# Revit family: QF_ELECTROLUXPROFESSIONAL_1LSNTG_WS6-28_E
name_source: partatom
category: Attrezzature speciali
units: mm (PartAtom-declared; Revit-internal decimal feet)

## family parameters
Basato su piano di lavoro = No
Condiviso = No
Punto di calcolo locali = No
Quota connettore circolare = Usa diametro
Sempre verticale = Sì
Taglio con vuoti quando caricato = No
Tipo di parte = Normale

## types (36) — shared parameters
Depth = 1030 mm  [stored 3.37927 ft]
Depth Actual = 1030 mm  [stored 3.37927 ft]
Height = 1430.8 mm  [stored 4.69423 ft]
Height Actual = 1430 mm  [stored 4.6916 ft]
Latent Heat Output = 0.0
Length Actual = 830 mm  [stored 2.7231 ft]
Modello = WS6-28
Produttore = Electrolux Professional
Sensible Heat Output = 0.0
URL = www.electroluxprofessional.com
Weight = 262
Width = 830 mm  [stored 2.7231 ft]
zero-valued in all types: Gas KW, Prospetto di default, Steam Pounds per Hour

## per-type parameters (varying)
| type | Cycle | Descrizione | Item Number | Phase | Volts | Watts |
| 9867930109 | 50 Hz | WASHER WS6-28 28KG EL 18KW 380-415/50/3N COMPASS PRO 6H01 ML 2xWATER POWDER+5xLIQ. VALV.OPEN SILVER 2.I/O DISCON. STOP | 1LSP3U | 3 | 415 V | 18800 W |
| 9867930201 | 50 Hz | WASHER WS6-28 28KG EL 18KW 380-415/50/3N COMPASS PRO 6G01 CH-EN 2xWATER POWDER EL.VALV.OPEN SILVER DISCON. STOP | 1LA23U | 3 | 415 V | 18800 W |
| 9867930106 | 50 Hz | WASHER WS6-28 28KG EL 18KW 380-415/50/3N COMPASS PRO 6H12 ML 2xWATER POWDER+5xLIQ. VALV.CLOSED SILVER 2.I/O DISCON. STOP | 1LSP60 | 3 | 415 V | 18800 W |
| 9867930261 | 50 Hz | WASHER WS6-28 28KG EL 18KW 440/50/3 COMPASS PRO 6G01 ML 2xWATER POWDER+5xLIQ. VALV.CLOSED SILVER 2.I/O TRAFO DISCON. STO | 1L0HDT | 3 | 440 V | 18800 W |
| 9867930149 | 60 Hz | WASHER WS6-28 28KG NO HEAT 208-240/60/1 COMPASS PRO 6G01 ML 2xWATER POWDER+5xLIQ. VALV.CLOSED SILVER 2.I/O STOP | 1LSPAS | 1 | 240 V | 1100 W |
| 9867930156 | 50 Hz | WASHER WS6-28 28KG NO HEAT 220-240/50/1N COMPASS PRO 6L01 ML 2xWATER POWDER+5xLIQ. VALV.OPEN SST/SILVER EXT.PM. 2.I/O DI | 1LSPBK | 1 | 240 V | 1100 W |
| 9867930241 | 60 Hz | WASHER WS6-28 28KG EL 18KW 208-240/60/3 COMPASS PRO 6H12 ML 2xWATER POWDER+5xLIQ. VALV.OPEN SST 2.I/O DISCON. STOP | 1LSPST | 3 | 240 V | 18800 W |
| 9867930214 | 60 Hz | WASHER WS6-28 28KG EL 18KW 208-240/60/3 COMPASS PRO 6G01 ML 2xWATER POWDER+5xLIQ. VALV.CLOSED SILVER 2.I/O DISCON. STOP | 1L0GXS | 3 | 240 V | 18800 W |
| 9867930186 | 60 Hz | WASHER WS6-28 28KG NO HEAT 208-240/60/1 COMPASS PRO 6L01 ML 2xWATER POWDER+5xLIQ. VALV.OPEN SILVER ELS-NETW. 2.I/O | 1LSPEA | 1 | 240 V | 1100 W |
| 9867930183 | 50 Hz | WASHER WS6-28 28KG EL 18KW 380-415/50/3 COMPASS PRO 6G07 ML 2xWATER POWDER+5xLIQ. VALV.OPEN SST/SILVER 2.I/O TRAFO DISCO | 1L0GLF | 3 | 415 V | 18800 W |
| 9867930207 | 60 Hz | WASHER WS6-28 28KG EL 18KW 380-415/60/3 COMPASS PRO 6G01 ML 2xWATER POWDER VALV.OPEN SILVER TRAFO DISCON. STOP | 1L827R | 3 | 415 V | 18800 W |
| 9867930257 | 50 Hz | WASHER WS6-28 28KG EL 18KW 380-415/50/3N COMPASS PRO 6G01 ML 2xWATER POWDER+5xLIQ. VALV.CLOSED SILVER 2.I/O DISCON. STOP | 1LM0AT | 3 | 415 V | 18800 W |
| 9867930130 | 60 Hz | WASHER WS6-28 28KG EL 18KW 440/60/3 COMPASS PRO 6G07 ML 2xWATER POWDER+5xLIQ. VALV.OPEN SST/SILVER 2.I/O TRAFO DISCON. S | 1L0GBR | 3 | 440 V | 18800 W |
| 9867930110 | 50 Hz | WASHER WS6-28 28KG NO HEAT 220-240/50/1N COMPASS PRO 6G05 ML 2xWATER POWDER+5xLIQ. VALV.OPEN SST/SILVER 2.I/O DISCON. ST | 1LSP62 | 1 | 240 V | 1100 W |
| 9867930135 | 50 Hz | WASHER WS6-28 28KG MOP 18KW 380-415/50/3N COMPASS PRO 6F01 ML 2xWATER POWDER+ED EL.VALV.OPEN SST DISCON. STOP LID | 1L0GCX | 3 | 415 V | 18800 W |
| 9867930180 | 60 Hz | WASHER WS6-28 28KG EL 18KW 380-415/60/3 COMPASS PRO 6G07 ML 2xWATER POWDER+ED VALV.OPEN SST/SILVER TRAFO DISCON. STOP | 1LA21Z | 3 | 415 V | 18800 W |
| 9867930105 | 50 Hz | WASHER WS6-28 28KG EL 18KW 380-415/50/3N COMPASS PRO 6G01 ML 2xWATER POWDER VALV.OPEN SILVER DISCON. STOP | 1L824J | 3 | 415 V | 18800 W |
| 9867930175 | 50 Hz | WASHER WS6-28 28KG NO HEAT 220-240/50/1N COMPASS PRO 6L01 ML 2xWATER POWDER+5xLIQ. VALV.OPEN SILVER ELS-NETW. 2.I/O DISC | 1L0GJR | 1 | 240 V | 1100 W |
| 9867930108 | 50 Hz | WASHER WS6-28 28KG EL 18KW 380-415/50/3N COMPASS PRO 6G01 ML 2xWATER POWDER+5xLIQ. VALV.OPEN SILVER 2.I/O DISCON. STOP | 1LSP61 | 3 | 415 V | 18800 W |
| 9867930145 | 50 Hz | WASHER WS6-28 28KG NO HEAT 200/50/60/3 COMPASS PRO 6L41 JP,EN 2xWATER 5xLIQ. VALV.OPEN SILVER 2.I/O DISCON. | 1LSP8W | 3 | 200 V | 1100 W |
| 9867930252 | 50 Hz | WASHER WS6-28 28KG EL 18KW 380-415/50/3N COMPASS PRO 6G01 ML 2xWATER POWDER+5xLIQ. VALV.OPEN SST 2.I/O DISCON. STOP | 1L0HBG | 3 | 415 V | 18800 W |
| 9867930235 | 50 Hz | WASHER WS6-28 28KG NO HEAT 220-240/50/1N COMPASS PRO 6L01 ML 2xWATER POWDER+5xLIQ. VALV.OPEN SILVER 2.I/O DISCON. | 1L82AH | 1 | 240 V | 1100 W |
| 9867930198 | 50 Hz | WASHER WS6-28 28KG NO HEAT 220-240/50/1N COMPASS PRO 6L01 ML 2xWATER POWDER+5xLIQ. VALV.OPEN SST/SILVER ELS-NETW. EXT.PM | 1L8269 | 1 | 240 V | 1100 W |
| 9867930245 | 60 Hz | WASHER WS6-28 28KG EL 18KW 480/60/3 COMPASS PRO 6G07 ML 2xWATER POWDER+5xLIQ. VALV.OPEN SST/SILVER 2.I/O TRAFO DISCON. S | 1L0H37 | 3 | 480 V | 18800 W |
| 9867930182 | 60 Hz | WASHER WS6-28 28KG EL 18KW 380-415/60/3 COMPASS PRO 6G07 ML 2xWATER POWDER+5xLIQ. VALV.OPEN SST/SILVER 2.I/O TRAFO DISCO | 1LA22G | 3 | 415 V | 18800 W |
| 9867930200 | 50 Hz | WASHER WS6-28 28KG EL 18KW 380-415/50/3N COMPASS PRO 6G01 ML 2xWATER POWDER+5xLIQ. EL.VALV.OPEN SST/SILVER 2.I/O DISCON. | 1LA238 | 3 | 415 V | 18800 W |
| 9867930107 | 50 Hz | WASHER WS6-28 28KG EL 18KW 380-415/50/3N COMPASS PRO 6G01 ML 2xWATER POWDER+5xLIQ. VALV.OPEN SST/SILVER 2.I/O DISCON. ST | 1LSP3T | 3 | 415 V | 18800 W |
| 9867930157 | 50 Hz | WASHER WS6-28 28KG NO HEAT 220-240/50/1N COMPASS PRO 6L01 ML 2xWATER POWDER+5xLIQ. VALV.OPEN SILVER EXT.PM. 2.I/O DISCON | 1LSPBT | 1 | 240 V | 1100 W |
| 9867930240 | 50 Hz | WASHER WS6-28 28KG NO HEAT 220-240/50/1N COMPASS PRO 6G01 ML 2xWATER POWDER+5xLIQ. VALV.OPEN SILVER 2.I/O DISCON. STOP | 1LSPSE | 1 | 240 V | 1100 W |
| 9867930197 | 50 Hz | WASHER WS6-28 28KG MOP 18KW 380-415/220-240/50/3N/3 COMPASS PRO 6M14 ML 2xWATER POWDER+5xLIQ. EL.VALV.OPEN SILVER 2.I/O | 1L0GTX | 3 | 415 V | 18800 W |
| 9867930208 | 50 Hz | WASHER WS6-28 28KG NO HEAT 200/50/60/3 COMPASS PRO 6L41 JP,EN 2xWATER POWDER+5xLIQ. VALV.OPEN SILVER 2.I/O DISCON. | 1L827S | 3 | 200 V | 1100 W |
| 9867930278 | 50 Hz | WASHER WS6-28 28KG EL 18KW 380-415/220-240/50/3N/3 COMPASS PRO 6G01 ML 2xWATER POWDER+5xLIQ. VALV.OPEN SILVER 2.I/O DISC | 1L0HJ8 | 3 | 415 V | 18800 W |
| 9867930268 | 60 Hz | WASHER WS6-28 28KG NO HEAT 220/60/3 COMPASS PRO 6L01 ML 2xWATER POWDER VALV.OPEN SILVER DISCON. | 1LT68Z | 3 | 220 V | 1100 W |
| 9867930248 | 60 Hz | WASHER WS6-28 28KG EL 18KW 480/60/3 COMPASS PRO 6G01 ML 2xWATER POWDER+5xLIQ. VALV.OPEN SILVER 2.I/O TRAFO DISCON. STOP | 1L0H8L | 3 | 480 V | 18800 W |
| 9867930213 | 50 Hz | WASHER WS6-28 28KG NO HEAT 200/50/60/3 COMPASS PRO 6L41 JP,EN 2xWATER 5xLIQ. VALV.OPEN SST/SILVER 2.I/O DISCON. | 1L0GXR | 3 | 200 V | 1100 W |
| 9867930283 | 50 Hz | WASHER WS6-28 28KG EL 18KW 380-415/50/3N COMPASS PRO 6G01 ML 2xWATER POWDER VALV.OPEN SST/SILVER DISCON. STOP | 1L0HK2 | 3 | 415 V | 18800 W |

note: [stored X ft] marks values corroborated as IEEE doubles in the binary element streams (Revit-internal decimal feet)

## geometry (parser evidence)
native form markers: Sweep x4
no freeform markers — native parametric forms only
